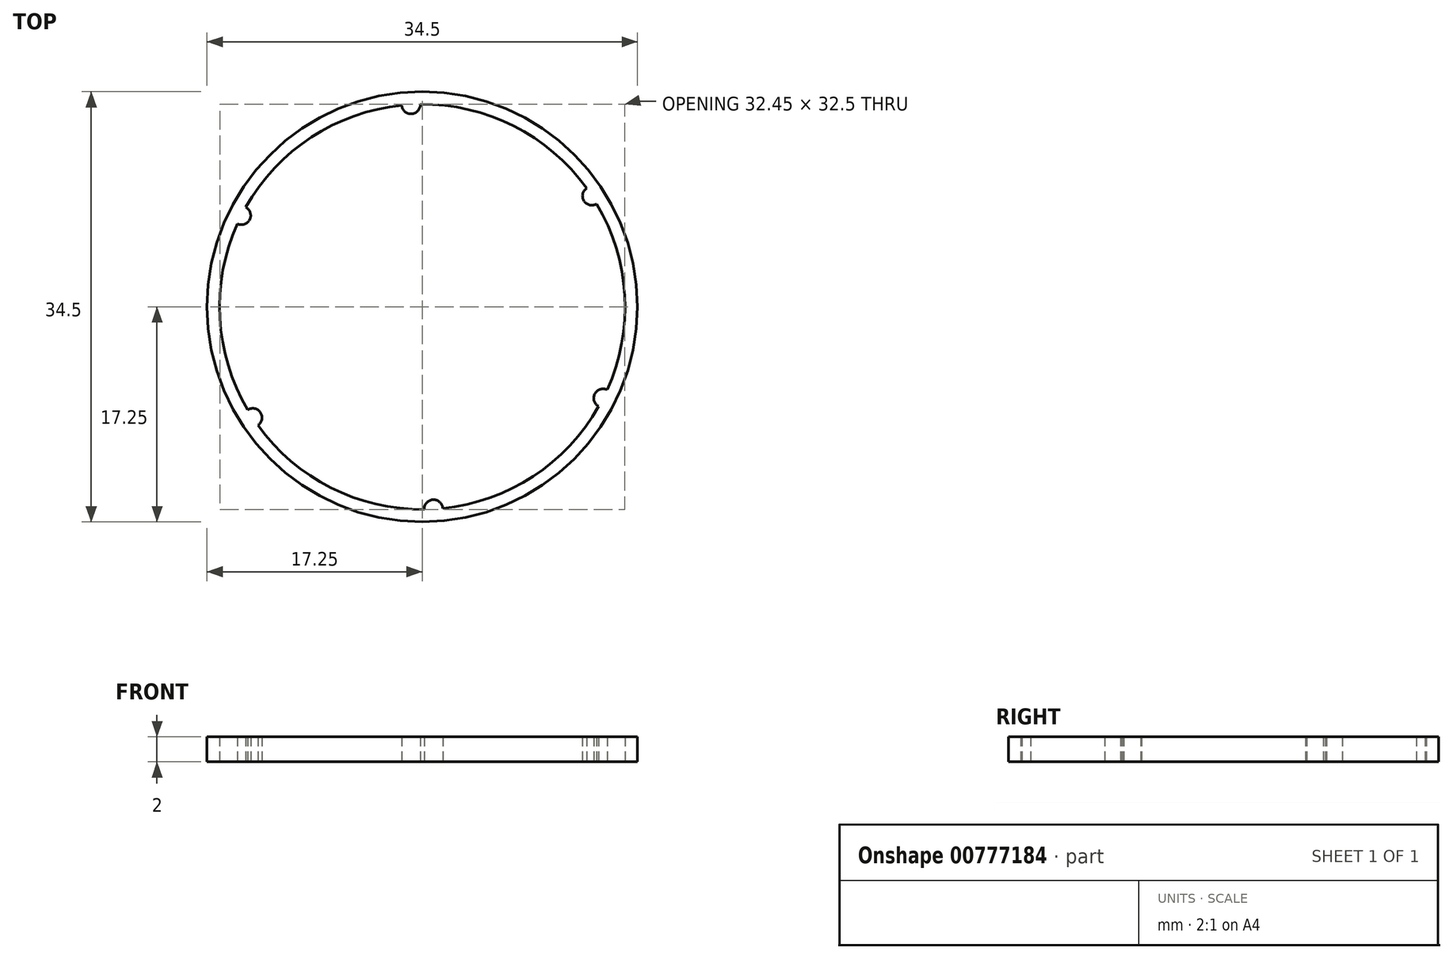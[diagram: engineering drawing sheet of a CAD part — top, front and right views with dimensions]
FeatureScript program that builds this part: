
annotation { "Feature Type Name" : "Feature", "Feature Type Description" : "" }
export const myFeature = defineFeature(function(context is Context, id is Id, definition is map)
    precondition{}
    {
        {
            var Q0;
            Q0=qCreatedBy(makeId("Top.planeOp"),FACE);
            var sketch = newSketch(context, id + "F0", { "sketchPlane" : qUnion([Q0])});
            skArc(sketch, "E0", {"start": v(-1.65, 16.17) * mm, "mid": v(-8.9, 13.6) * mm, "end": v(-14.15, 8) * mm});
            skCircle(sketch, "E1", {"center": v(0, 0) * mm, "radius": 17.25 * mm});
            skArc(sketch, "E2", {"start": v(-14.83, 6.65) * mm, "mid": v(-13.83, 7) * mm, "end": v(-14.15, 8) * mm});
            skArc(sketch, "E3.1.0", {"start": v(-13.17, -9.51) * mm, "mid": v(-12.97, -8.48) * mm, "end": v(-14, -8.26) * mm});
            skArc(sketch, "E3.2.0", {"start": v(1.65, -16.17) * mm, "mid": v(0.86, -15.48) * mm, "end": v(0.15, -16.25) * mm});
            skArc(sketch, "E3.3.0", {"start": v(14.83, -6.65) * mm, "mid": v(13.83, -7) * mm, "end": v(14.15, -8) * mm});
            skArc(sketch, "E3.4.0", {"start": v(13.17, 9.51) * mm, "mid": v(12.97, 8.48) * mm, "end": v(14, 8.26) * mm});
            skArc(sketch, "E3.5.0", {"start": v(-1.65, 16.17) * mm, "mid": v(-0.86, 15.48) * mm, "end": v(-0.15, 16.25) * mm});
            skArc(sketch, "E4.trimOffspring", {"start": v(13.17, 9.51) * mm, "mid": v(7.33, 14.5) * mm, "end": v(-0.15, 16.25) * mm});
            skArc(sketch, "E5.trimOffspring", {"start": v(14.83, -6.65) * mm, "mid": v(16.22, 0.9) * mm, "end": v(14, 8.26) * mm});
            skArc(sketch, "E6.trimOffspring", {"start": v(1.65, -16.17) * mm, "mid": v(8.9, -13.6) * mm, "end": v(14.15, -8) * mm});
            skArc(sketch, "E7.trimOffspring", {"start": v(-13.17, -9.51) * mm, "mid": v(-7.33, -14.5) * mm, "end": v(0.15, -16.25) * mm});
            skArc(sketch, "E8.trimOffspring", {"start": v(-14.83, 6.65) * mm, "mid": v(-16.22, -0.9) * mm, "end": v(-14, -8.26) * mm});
            skSolve(sketch);
        }
        {
            var Q0;
            Q0=makeQuery(id+"F0.imprint","IMPRINT",FACE,{"disambiguationData":[TD([[makeQuery(id+"F0.imprint","IMPRINT",EDGE,{"derivedFrom":sQuery(id+"F0.wireOp",EDGE,"E1")}),1.0]])]});
            extrude(context, id + "F1", {"entities" : qUnion([Q0]), "depth" : 2 * mm, "offsetDistance" : 25 * mm});
        }
    });
